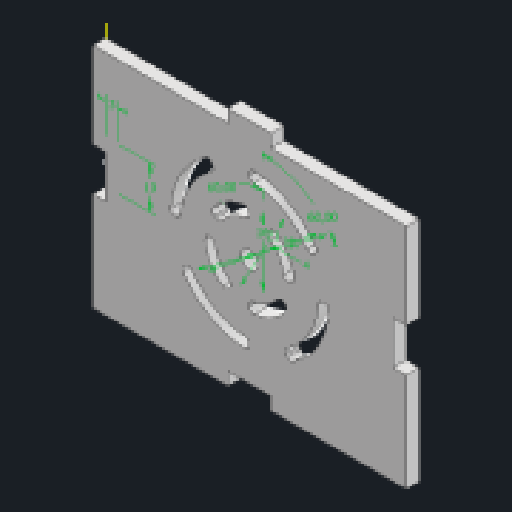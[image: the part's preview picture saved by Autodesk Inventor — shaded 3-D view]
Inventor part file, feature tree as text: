
AUTODESK INVENTOR PART (.ipt)
format: ipt  version: 2023 (Build 270158000, 158)  size: 230,400 bytes
history: native  units: mm
features: extrude x5, sketch x4, fillet x1, pattern_circular x1
ambient origin geometry x8: Origin, YZ Plane, XZ Plane, XY Plane, X Axis, Y Axis, Z Axis, Center Point
bodies: Solid1 (feature_tree)
feature tree (11):
  extrude  "Extrusion1"  Depth=56.0mm
  sketch  "Sketch2"  dims[d2=3.0mm d3=0.0mm d4=3.0mm d5=10.0mm]
  extrude  "Extrusion3"  Depth=3.0mm
  fillet  "Fillet1"  Radius=10.0mm
  pattern_circular  "Circular Pattern1"  [2 undecoded]
  extrude  "Extrusion6"  Depth=3.0mm
  sketch  "Sketch6"  dims[d7=16.0mm d8=21.0mm d9=32.0mm d10=37.0mm d11=60.0deg d12=60.0deg d15=1.0mm d16=10.0mm d17=0.0mm d18=40.0mm d19=360.0deg d31=10.0mm d32=3.0mm d33=36.5mm d34=10.0mm d35=3.0mm d36=3.0mm d37=10.0mm d38=3.0mm d39=10.0mm d40=0.0mm d41=0.0mm d42=3.0mm d43=0.0mm d44=0.0mm d45=0.0mm]
  extrude  "Extrusion7"  Depth=3.0mm
  extrude  "Extrusion8"  TaperAngle=60.0deg  [1 undecoded]
  sketch  "Sketch1"  dims[d0=73.0mm d1=56.0mm]
  sketch  "Sketch5"  dims[d6=4.0mm]
note: 3 required parameter values undecoded (feature->parameter linkage not recoverable at this tier; creation-order binding heuristic only, values carry confidence <= 0.55)
